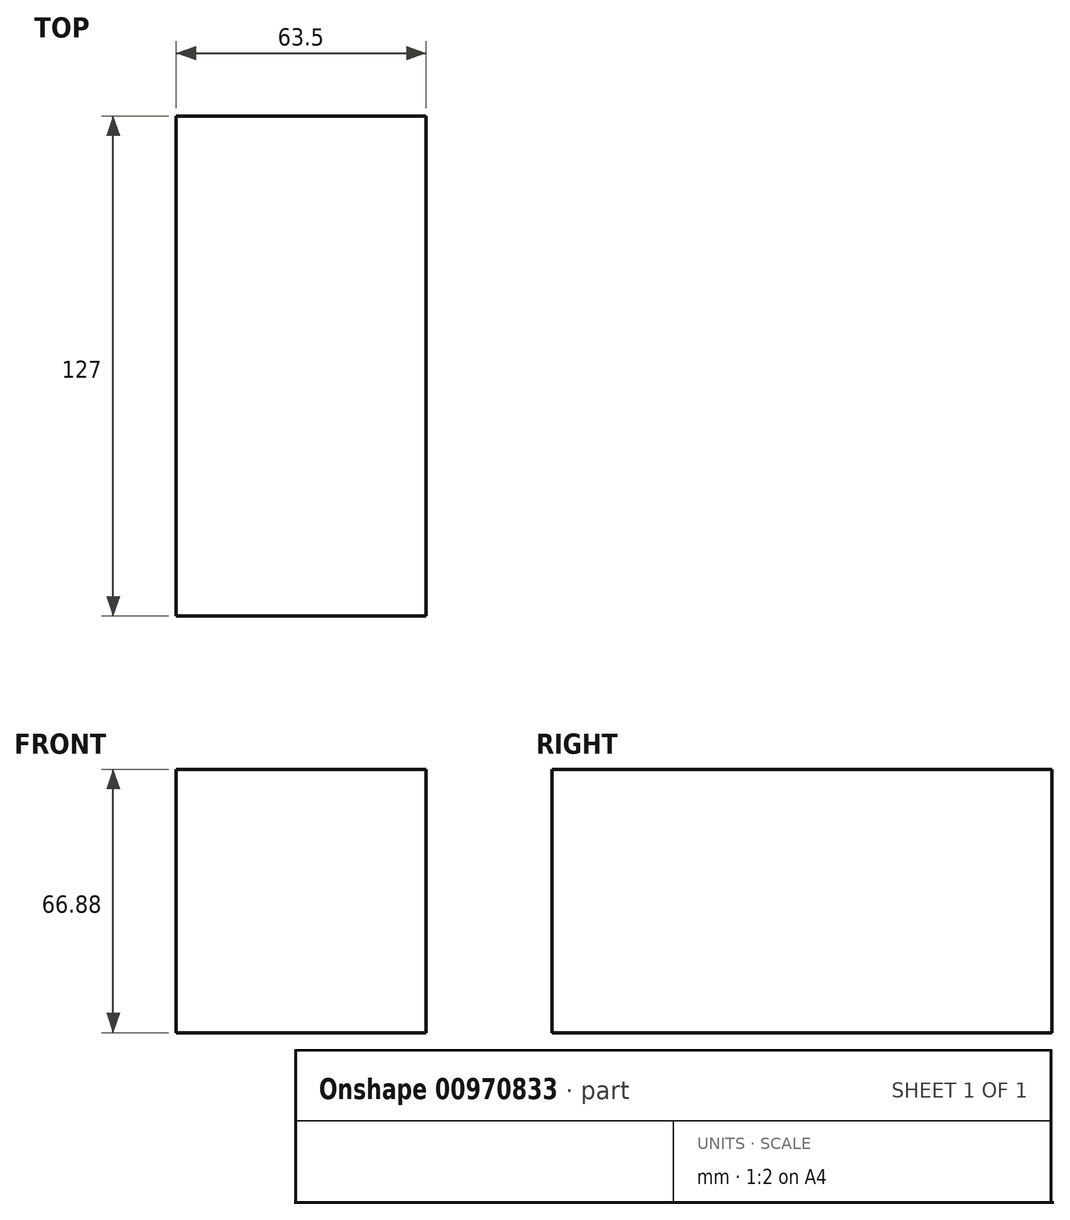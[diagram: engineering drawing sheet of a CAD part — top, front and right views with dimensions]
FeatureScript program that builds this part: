
annotation { "Feature Type Name" : "Feature", "Feature Type Description" : "" }
export const myFeature = defineFeature(function(context is Context, id is Id, definition is map)
    precondition{}
    {
        {
            var Q0;
            Q0=qCreatedBy(makeId("Front.planeOp"),FACE);
            var sketch = newSketch(context, id + "F0", { "sketchPlane" : qUnion([Q0])});
            skLineSegment(sketch, "E0.bottom", {"start": v(-81.12, 59.78) * mm, "end": v(45.88, 59.78) * mm});
            skLineSegment(sketch, "E0.top", {"start": v(-81.12, -67.22) * mm, "end": v(45.88, -67.22) * mm});
            skLineSegment(sketch, "E0.left", {"start": v(-81.12, 59.78) * mm, "end": v(-81.12, -67.22) * mm});
            skLineSegment(sketch, "E0.right", {"start": v(45.88, 59.78) * mm, "end": v(45.88, -67.22) * mm});
            skLineSegment(sketch, "E1", {"start": v(-17.62, 59.78) * mm, "end": v(-17.62, -67.22) * mm});
            skLineSegment(sketch, "E2", {"start": v(-81.12, -7.1) * mm, "end": v(45.88, -7.1) * mm});
            skSolve(sketch);
        }
        {
            var Q0;
            {var subQ0=sQuery(id+"F0.wireOp",EDGE,"E0.right");var subQ1=sQuery(id+"F0.wireOp",EDGE,"E0.bottom");var subQ2=makeQuery(id+"F0.imprint","INTERSECT",VERTEX,{"derivedFrom":[subQ1,subQ0]});Q0=makeQuery(id+"F0.imprint","IMPRINT",FACE,{"disambiguationData":[TD([[makeQuery(id+"F0.imprint","IMPRINT",EDGE,{"disambiguationData":[TD([[subQ2,1.0]])],"derivedFrom":subQ1}),-1.0]])]});}
            extrude(context, id + "F1", {"entities" : qUnion([Q0]), "depth" : 127 * mm, "offsetDistance" : 25.4 * mm});
        }
        {
            var Q0;
            Q0=makeQuery(id+"F1.opExtrude","SWEPT_FACE",FACE,{"disambiguationData":[OSD([sQuery(id+"F0.wireOp",EDGE,"E0.bottom")])]});
            extrude(context, id + "F2", {"entities" : qUnion([Q0]), "operationType" : NewBodyOperationType.ADD, "oppositeDirection" : true, "depth" : 25 * mm, "offsetDistance" : 25 * mm});
        }
    });
